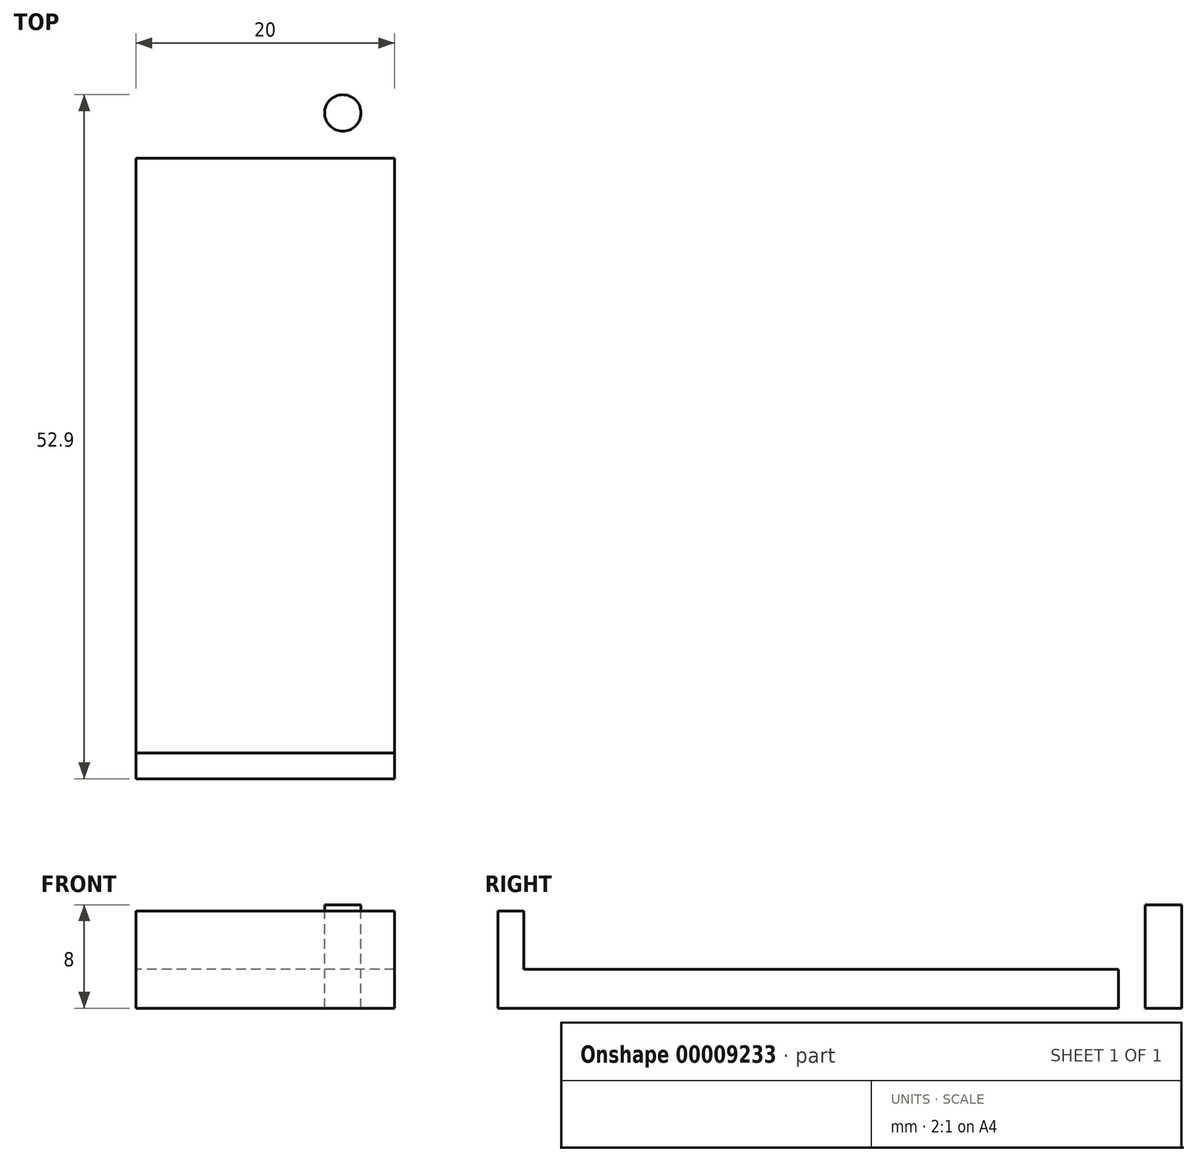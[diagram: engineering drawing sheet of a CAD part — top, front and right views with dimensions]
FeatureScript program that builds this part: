
annotation { "Feature Type Name" : "Feature", "Feature Type Description" : "" }
export const myFeature = defineFeature(function(context is Context, id is Id, definition is map)
    precondition{}
    {
        {
            var Q0;
            Q0=qCreatedBy(makeId("Right.planeOp"),FACE);
            var sketch = newSketch(context, id + "F0", { "sketchPlane" : qUnion([Q0])});
            skLineSegment(sketch, "E0", {"start": v(34.28, 5.69) * mm, "end": v(34.28, -2.31) * mm});
            skLineSegment(sketch, "E1", {"start": v(34.28, -2.31) * mm, "end": v(-20.72, -2.31) * mm});
            skLineSegment(sketch, "E2", {"start": v(27.28, 0.69) * mm, "end": v(27.28, 5.69) * mm});
            skLineSegment(sketch, "E3", {"start": v(34.28, 5.69) * mm, "end": v(27.28, 5.69) * mm});
            skLineSegment(sketch, "E4", {"start": v(-20.72, -2.31) * mm, "end": v(-20.72, 5.19) * mm});
            skLineSegment(sketch, "E5", {"start": v(-20.72, 5.19) * mm, "end": v(-18.72, 5.19) * mm});
            skLineSegment(sketch, "E6", {"start": v(-18.72, 5.19) * mm, "end": v(-18.72, 0.69) * mm});
            skLineSegment(sketch, "E7", {"start": v(-18.72, 0.69) * mm, "end": v(27.28, 0.69) * mm});
            skSolve(sketch);
        }
        {
            var Q0;
            Q0 = qSketchRegion(id + "F0", true);
            extrude(context, id + "F1", {"entities" : qUnion([Q0]), "endBound" : BoundingType.SYMMETRIC, "depth" : 20 * mm});
        }
        {
            var Q0;
            Q0=makeQuery(id+"F1.opExtrude","SWEPT_FACE",FACE,{"disambiguationData":[OSD([sQuery(id+"F0.wireOp",EDGE,"E3")])]});
            var sketch = newSketch(context, id + "F2", { "sketchPlane" : qUnion([Q0])});
            skCircle(sketch, "E8", {"center": v(-6, 30.78) * mm, "radius": 1.4 * mm});
            skCircle(sketch, "E9.0.MirrorC", {"center": v(6, 30.78) * mm, "radius": 1.4 * mm});
            skSolve(sketch);
        }
        {
            var Q0;
            Q0=makeQuery(id+"F2.imprint","IMPRINT",FACE,{"disambiguationData":[TD([[makeQuery(id+"F2.imprint","IMPRINT",EDGE,{"derivedFrom":sQuery(id+"F2.wireOp",EDGE,"E8")}),1.0]])]});
            var Q1;
            Q1=makeQuery(id+"F2.imprint","IMPRINT",FACE,{"disambiguationData":[TD([[makeQuery(id+"F2.imprint","IMPRINT",EDGE,{"derivedFrom":sQuery(id+"F2.wireOp",EDGE,"E9.0.MirrorC")}),-1.0]])]});
            extrude(context, id + "F3", {"entities" : qUnion([Q0, Q1]), "operationType" : NewBodyOperationType.REMOVE, "oppositeDirection" : true, "depth" : 25 * mm});
        }
    });
